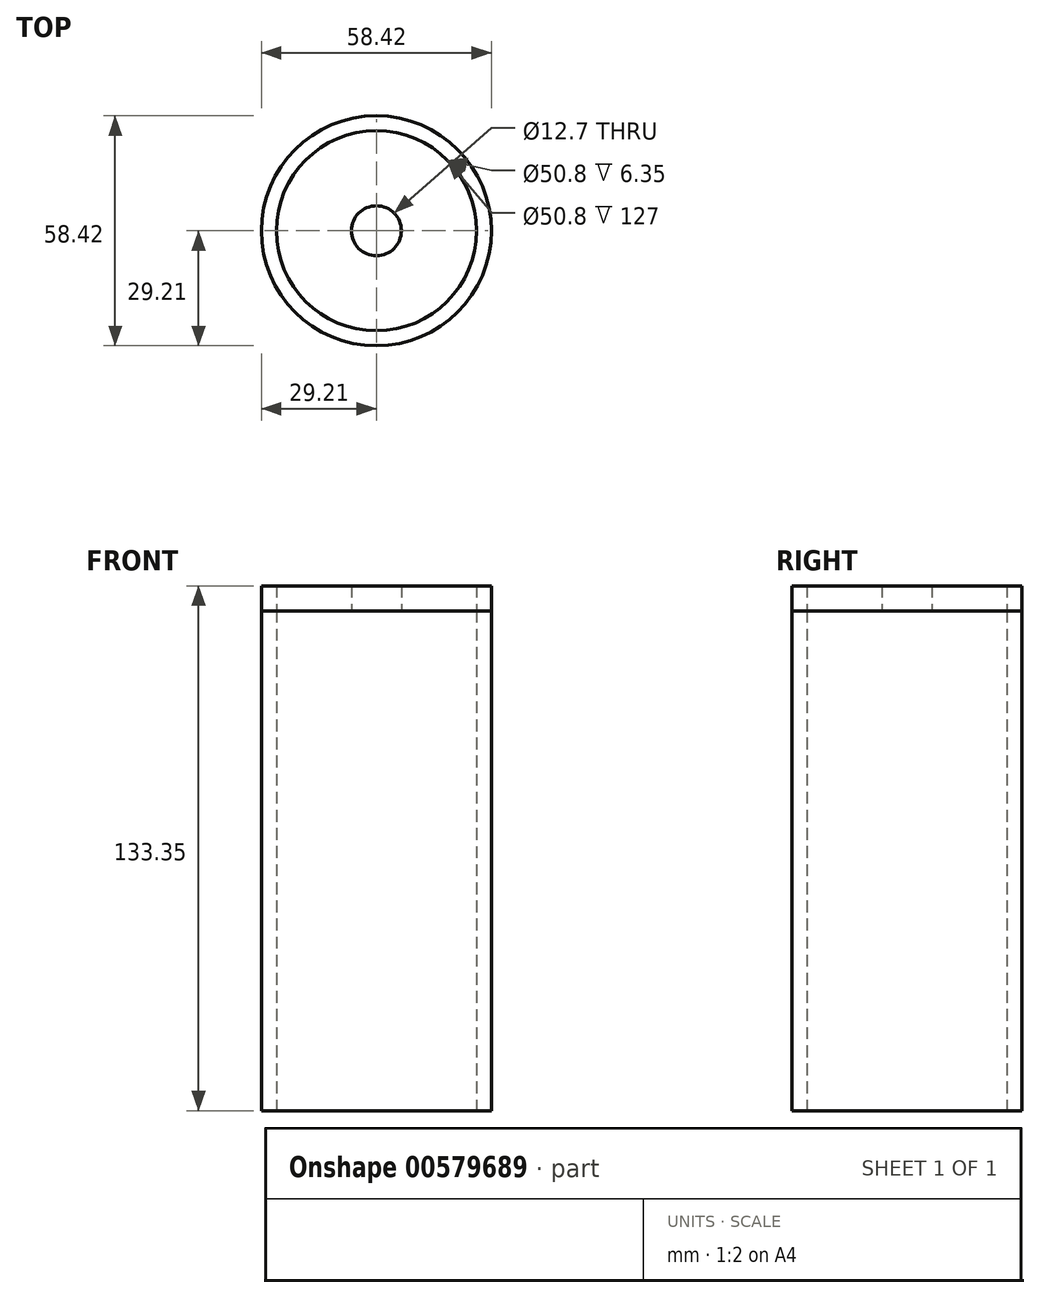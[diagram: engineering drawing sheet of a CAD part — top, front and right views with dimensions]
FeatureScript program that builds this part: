
annotation { "Feature Type Name" : "Feature", "Feature Type Description" : "" }
export const myFeature = defineFeature(function(context is Context, id is Id, definition is map)
    precondition{}
    {
        {
            var Q0;
            Q0=qCreatedBy(makeId("Top.planeOp"),FACE);
            var sketch = newSketch(context, id + "F0", { "sketchPlane" : qUnion([Q0])});
            skCircle(sketch, "E0", {"center": v(0, 0) * mm, "radius": 25.4 * mm});
            skCircle(sketch, "E1", {"center": v(0, 0) * mm, "radius": 29.21 * mm});
            skSolve(sketch);
        }
        {
            var Q0;
            Q0=makeQuery(id+"F0.imprint","IMPRINT",FACE,{"disambiguationData":[TD([[makeQuery(id+"F0.imprint","IMPRINT",EDGE,{"derivedFrom":sQuery(id+"F0.wireOp",EDGE,"E0")}),-1.0]])]});
            extrude(context, id + "F1", {"entities" : qUnion([Q0]), "depth" : 127 * mm, "offsetDistance" : 25.4 * mm});
        }
        {
            var Q0;
            Q0=makeQuery(id+"F1.opExtrude","CAP_FACE",FACE,{"disambiguationData":[OSD([sQuery(id+"F0.wireOp",EDGE,"E0"),sQuery(id+"F0.wireOp",EDGE,"E1")])],"isStart":false});
            var sketch = newSketch(context, id + "F2", { "sketchPlane" : qUnion([Q0])});
            skCircle(sketch, "E2", {"center": v(0, 0) * mm, "radius": 29.21 * mm});
            skCircle(sketch, "E3", {"center": v(0, 0) * mm, "radius": 6.35 * mm});
            skSolve(sketch);
        }
        {
            var Q0;
            Q0=makeQuery(id+"F2.imprint","IMPRINT",FACE,{"disambiguationData":[TD([[makeQuery(id+"F2.imprint","IMPRINT",EDGE,{"derivedFrom":makeQuery(id+"F1.opExtrude","CAP_EDGE",EDGE,{"disambiguationData":[OSD([sQuery(id+"F0.wireOp",EDGE,"E0")])],"isStart":false})}),1.0]])]});
            extrude(context, id + "F3", {"entities" : qUnion([Q0]), "depth" : 6.35 * mm, "offsetDistance" : 25.4 * mm});
        }
        {
            var Q0;
            Q0=makeQuery(id+"F1.opExtrude","CAP_FACE",FACE,{"disambiguationData":[OSD([sQuery(id+"F0.wireOp",EDGE,"E0"),sQuery(id+"F0.wireOp",EDGE,"E1")])],"isStart":false});
            extrude(context, id + "F4", {"entities" : qUnion([Q0]), "depth" : 6.35 * mm, "offsetDistance" : 25.4 * mm});
        }
    });
